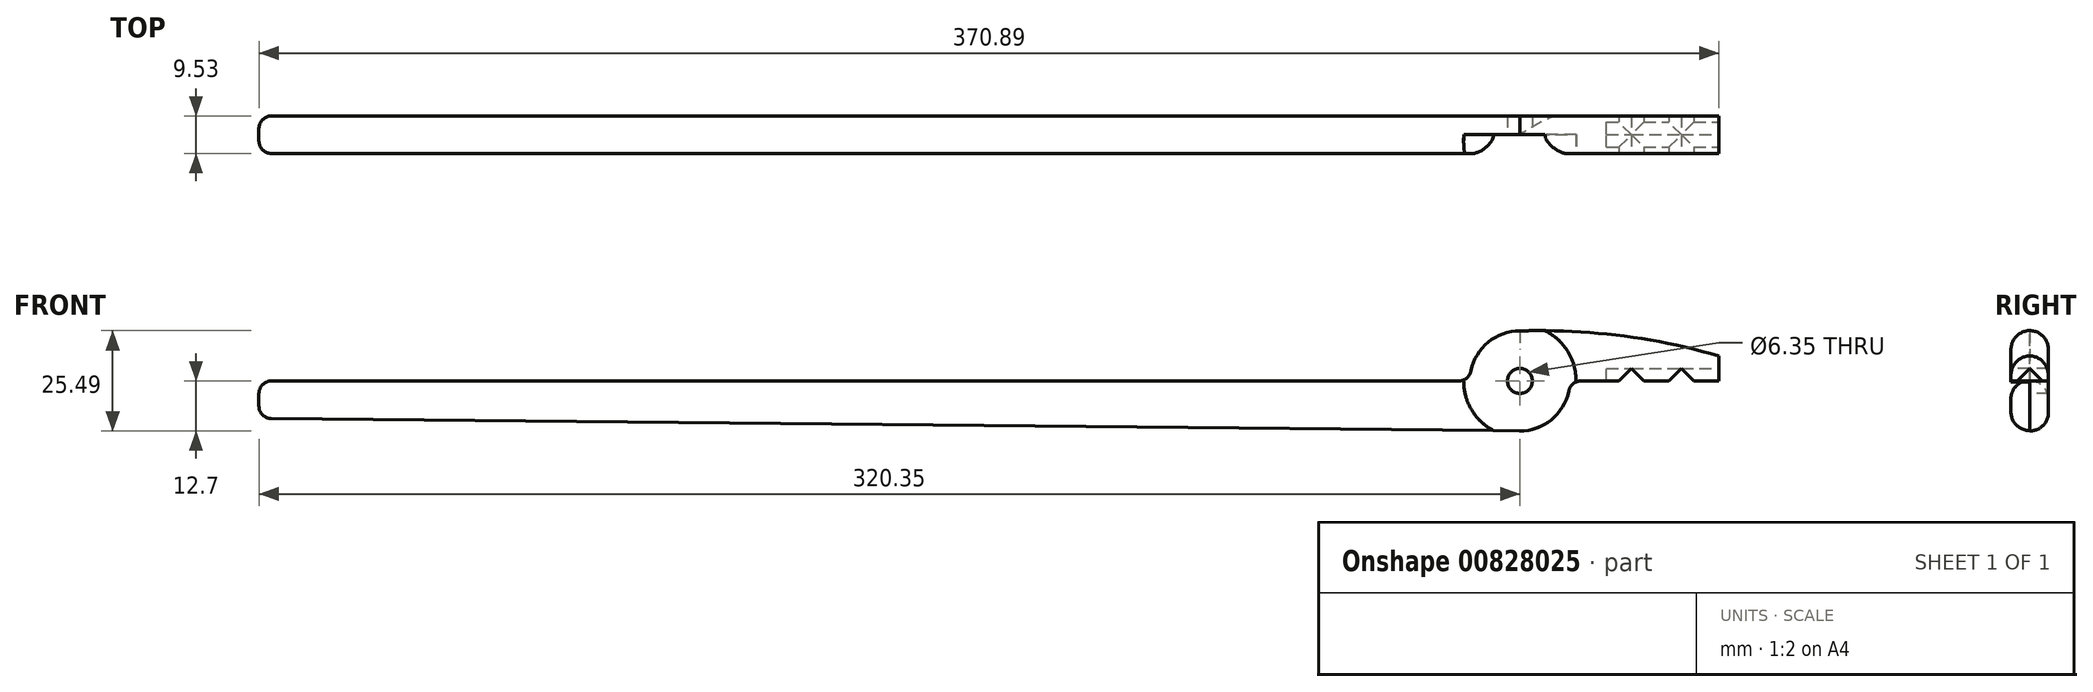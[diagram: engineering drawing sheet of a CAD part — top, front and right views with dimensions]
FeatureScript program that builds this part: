
annotation { "Feature Type Name" : "Feature", "Feature Type Description" : "" }
export const myFeature = defineFeature(function(context is Context, id is Id, definition is map)
    precondition{}
    {
        {
            var Q0;
            Q0=qCreatedBy(makeId("Front.planeOp"),FACE);
            var sketch = newSketch(context, id + "F0", { "sketchPlane" : qUnion([Q0])});
            skArc(sketch, "E0", {"start": v(-0.13, -12.7) * mm, "mid": v(7.98, -9.88) * mm, "end": v(12.44, -2.54) * mm});
            skLineSegment(sketch, "E1", {"start": v(-15.55, 0) * mm, "end": v(-320.35, 0) * mm});
            skLineSegment(sketch, "E2", {"start": v(-320.35, 0) * mm, "end": v(-320.35, -9.53) * mm});
            skLineSegment(sketch, "E3", {"start": v(-320.35, -9.53) * mm, "end": v(0, -12.7) * mm});
            skArc(sketch, "E4", {"start": v(-15.55, 0) * mm, "mid": v(-13.55, 0.72) * mm, "end": v(-12.44, 2.54) * mm});
            skPoint(sketch, "E5.orphan", {"position": v(-12.7, 0) * mm});
            skArc(sketch, "E6", {"start": v(50.54, 6.35) * mm, "mid": v(25.52, 11.52) * mm, "end": v(0, 12.7) * mm});
            skLineSegment(sketch, "E7", {"start": v(50.54, 6.35) * mm, "end": v(50.54, 0) * mm});
            skLineSegment(sketch, "E8", {"start": v(50.54, 0) * mm, "end": v(15.55, 0) * mm});
            skArc(sketch, "E9.trimOffspring", {"start": v(0, 12.7) * mm, "mid": v(-8.03, 9.84) * mm, "end": v(-12.44, 2.54) * mm});
            skArc(sketch, "E10", {"start": v(15.55, 0) * mm, "mid": v(13.55, -0.72) * mm, "end": v(12.44, -2.54) * mm});
            skSolve(sketch);
        }
        {
            var Q0;
            {var subQ1=sQuery(id+"F0.wireOp",EDGE,"E0");Q0=makeQuery(id+"F0.imprint","IMPRINT",FACE,{"disambiguationData":[TD([[makeQuery(id+"F0.imprint","IMPRINT",EDGE,{"derivedFrom":subQ1}),1.0]])]});}
            extrude(context, id + "F1", {"entities" : qUnion([Q0]), "depth" : 9.52 * mm, "offsetDistance" : 25.4 * mm});
        }
        {
            var Q0;
            Q0=makeQuery(id+"F1.opExtrude","SWEPT_FACE",FACE,{"disambiguationData":[OSD([sQuery(id+"F0.wireOp",EDGE,"E7")])]});
            var sketch = newSketch(context, id + "F2", { "sketchPlane" : qUnion([Q0])});
            skLineSegment(sketch, "E11", {"start": v(-7.94, 0) * mm, "end": v(-4.76, 3.17) * mm});
            skPoint(sketch, "E11.endSnap0", {"position": v(-4.76, 6.35) * mm});
            skLineSegment(sketch, "E12", {"start": v(-4.76, 3.17) * mm, "end": v(-1.59, 0) * mm});
            skLineSegment(sketch, "E13", {"start": v(-7.94, 0) * mm, "end": v(-1.59, 0) * mm});
            skSolve(sketch);
        }
        {
            var Q0;
            Q0=makeQuery(id+"F2.imprint","IMPRINT",FACE,{"disambiguationData":[TD([[makeQuery(id+"F2.imprint","IMPRINT",EDGE,{"derivedFrom":sQuery(id+"F2.wireOp",EDGE,"E11")}),-1.0]])]});
            extrude(context, id + "F3", {"entities" : qUnion([Q0]), "operationType" : NewBodyOperationType.REMOVE, "oppositeDirection" : true, "depth" : 28.57 * mm, "offsetDistance" : 25.4 * mm});
        }
        {
            var Q0;
            Q0=makeQuery(id+"F1.opExtrude","CAP_FACE",FACE,{"disambiguationData":[OSD([sQuery(id+"F0.wireOp",EDGE,"E0"),sQuery(id+"F0.wireOp",EDGE,"E1"),sQuery(id+"F0.wireOp",EDGE,"E2"),sQuery(id+"F0.wireOp",EDGE,"E3"),sQuery(id+"F0.wireOp",EDGE,"E4"),sQuery(id+"F0.wireOp",EDGE,"E6"),sQuery(id+"F0.wireOp",EDGE,"E7"),sQuery(id+"F0.wireOp",EDGE,"E8"),sQuery(id+"F0.wireOp",EDGE,"E9.trimOffspring"),sQuery(id+"F0.wireOp",EDGE,"E10")])],"isStart":false});
            var sketch = newSketch(context, id + "F4", { "sketchPlane" : qUnion([Q0])});
            skLineSegment(sketch, "E14", {"start": v(44.2, 0) * mm, "end": v(41.02, 3.18) * mm});
            skLineSegment(sketch, "E15", {"start": v(41.02, 3.18) * mm, "end": v(37.84, 0) * mm});
            skLineSegment(sketch, "E16", {"start": v(37.84, 0) * mm, "end": v(44.2, 0) * mm});
            skLineSegment(sketch, "E17", {"start": v(41.02, 3.18) * mm, "end": v(41.02, 0) * mm, "construction": true});
            skLineSegment(sketch, "E18.1.0.0", {"start": v(28.32, 3.18) * mm, "end": v(25.14, 0) * mm});
            skLineSegment(sketch, "E18.1.0.1", {"start": v(31.5, 0) * mm, "end": v(28.32, 3.17) * mm});
            skLineSegment(sketch, "E18.1.0.2", {"start": v(25.14, 0) * mm, "end": v(31.5, 0) * mm});
            skLineSegment(sketch, "E18.direction1", {"start": v(37.84, 0) * mm, "end": v(25.14, 0) * mm, "construction": true});
            skSolve(sketch);
        }
        {
            var Q0;
            Q0=makeQuery(id+"F4.imprint","IMPRINT",FACE,{"disambiguationData":[TD([[makeQuery(id+"F4.imprint","IMPRINT",EDGE,{"derivedFrom":sQuery(id+"F4.wireOp",EDGE,"E18.1.0.0")}),1.0]])]});
            var Q1;
            Q1=makeQuery(id+"F4.imprint","IMPRINT",FACE,{"disambiguationData":[TD([[makeQuery(id+"F4.imprint","IMPRINT",EDGE,{"derivedFrom":sQuery(id+"F4.wireOp",EDGE,"E14")}),1.0]])]});
            extrude(context, id + "F5", {"entities" : qUnion([Q0, Q1]), "operationType" : NewBodyOperationType.REMOVE, "endBound" : BoundingType.THROUGH_ALL, "oppositeDirection" : true, "depth" : 25.4 * mm, "offsetDistance" : 25.4 * mm});
        }
        {
            var Q0;
            Q0=makeQuery(id+"F1.opExtrude","CAP_FACE",FACE,{"disambiguationData":[OSD([sQuery(id+"F0.wireOp",EDGE,"E0"),sQuery(id+"F0.wireOp",EDGE,"E1"),sQuery(id+"F0.wireOp",EDGE,"E2"),sQuery(id+"F0.wireOp",EDGE,"E3"),sQuery(id+"F0.wireOp",EDGE,"E4"),sQuery(id+"F0.wireOp",EDGE,"E6"),sQuery(id+"F0.wireOp",EDGE,"E7"),sQuery(id+"F0.wireOp",EDGE,"E8"),sQuery(id+"F0.wireOp",EDGE,"E9.trimOffspring"),sQuery(id+"F0.wireOp",EDGE,"E10")])],"isStart":false});
            var sketch = newSketch(context, id + "F6", { "sketchPlane" : qUnion([Q0])});
            skCircle(sketch, "E19", {"center": v(0, 0) * mm, "radius": 3.17 * mm});
            skSolve(sketch);
        }
        {
            var Q0;
            Q0=makeQuery(id+"F6.imprint","IMPRINT",FACE,{"disambiguationData":[TD([[makeQuery(id+"F6.imprint","IMPRINT",EDGE,{"derivedFrom":sQuery(id+"F6.wireOp",EDGE,"E19")}),1.0]])]});
            extrude(context, id + "F7", {"entities" : qUnion([Q0]), "operationType" : NewBodyOperationType.REMOVE, "endBound" : BoundingType.THROUGH_ALL, "oppositeDirection" : true, "depth" : 25.4 * mm, "offsetDistance" : 25.4 * mm});
        }
        {
            var Q0;
            Q0=makeQuery(id+"F1.opExtrude","CAP_EDGE",EDGE,{"disambiguationData":[OSD([sQuery(id+"F0.wireOp",EDGE,"E3")])],"isStart":false});
            var Q1;
            Q1=makeQuery(id+"F1.opExtrude","CAP_EDGE",EDGE,{"disambiguationData":[OSD([sQuery(id+"F0.wireOp",EDGE,"E3")])],"isStart":true});
            var Q2;
            Q2=makeQuery(id+"F1.opExtrude","CAP_EDGE",EDGE,{"disambiguationData":[OSD([sQuery(id+"F0.wireOp",EDGE,"E6")])],"isStart":false});
            var Q3;
            Q3=makeQuery(id+"F1.opExtrude","CAP_EDGE",EDGE,{"disambiguationData":[OSD([sQuery(id+"F0.wireOp",EDGE,"E6")])],"isStart":true});
            fillet(context, id + "F8", {"entities" : qUnion([Q0, Q1, Q2, Q3]), "radius" : 4.76 * mm, "allowEdgeOverflow" : false});
        }
        {
            var Q0;
            Q0=makeQuery(id+"F1.opExtrude","CAP_EDGE",EDGE,{"disambiguationData":[OSD([sQuery(id+"F0.wireOp",EDGE,"E1")])],"isStart":true});
            var Q1;
            Q1=makeQuery(id+"F1.opExtrude","CAP_EDGE",EDGE,{"disambiguationData":[OSD([sQuery(id+"F0.wireOp",EDGE,"E1")])],"isStart":false});
            fillet(context, id + "F9", {"entities" : qUnion([Q0, Q1]), "radius" : 4.76 * mm, "tangentPropagation" : true, "allowEdgeOverflow" : false});
        }
        {
            var Q0;
            Q0=makeQuery(id+"F1.opExtrude","SWEPT_FACE",FACE,{"disambiguationData":[OSD([sQuery(id+"F0.wireOp",EDGE,"E2")])]});
            fillet(context, id + "F10", {"entities" : qUnion([Q0]), "radius" : 3.17 * mm, "tangentPropagation" : true, "allowEdgeOverflow" : false});
        }
        {
            var Q0;
            Q0=makeQuery(id+"F1.opExtrude","CAP_FACE",FACE,{"disambiguationData":[OSD([sQuery(id+"F0.wireOp",EDGE,"E0"),sQuery(id+"F0.wireOp",EDGE,"E1"),sQuery(id+"F0.wireOp",EDGE,"E2"),sQuery(id+"F0.wireOp",EDGE,"E3"),sQuery(id+"F0.wireOp",EDGE,"E4"),sQuery(id+"F0.wireOp",EDGE,"E6"),sQuery(id+"F0.wireOp",EDGE,"E7"),sQuery(id+"F0.wireOp",EDGE,"E8"),sQuery(id+"F0.wireOp",EDGE,"E9.trimOffspring"),sQuery(id+"F0.wireOp",EDGE,"E10")])],"isStart":false});
            var sketch = newSketch(context, id + "F11", { "sketchPlane" : qUnion([Q0])});
            skCircle(sketch, "E20", {"center": v(0, 0) * mm, "radius": 14.29 * mm});
            skSolve(sketch);
        }
        {
            var Q0;
            Q0 = qSketchRegion(id + "F11", true);
            extrude(context, id + "F12", {"entities" : qUnion([Q0]), "operationType" : NewBodyOperationType.REMOVE, "oppositeDirection" : true, "depth" : 4.76 * mm, "offsetDistance" : 25.4 * mm});
        }
    });
